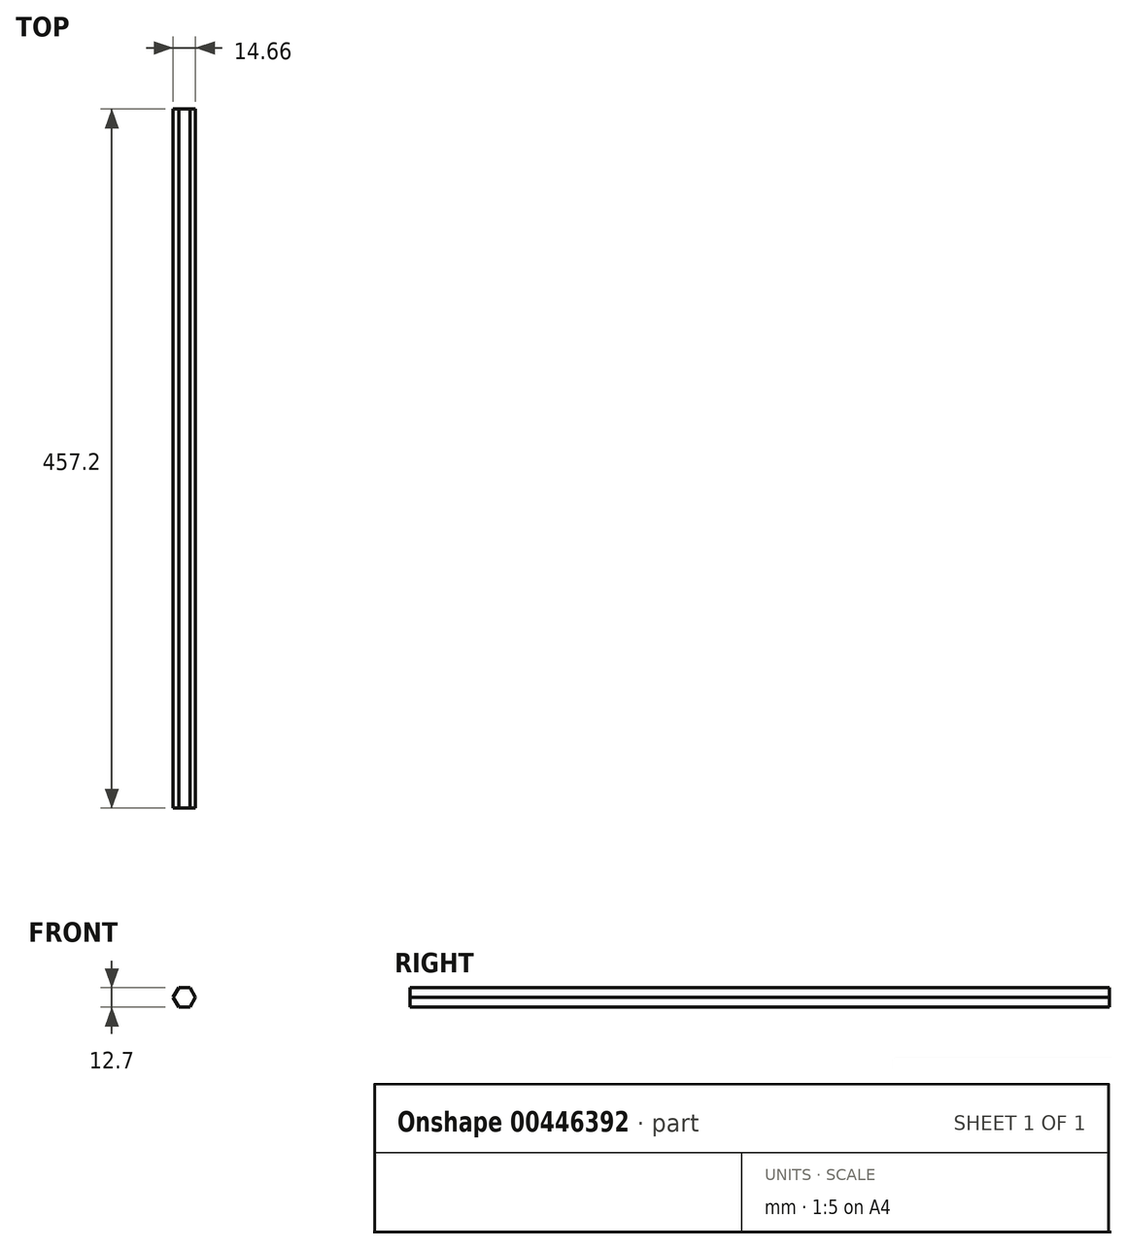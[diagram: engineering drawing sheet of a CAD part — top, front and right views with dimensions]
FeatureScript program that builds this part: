
annotation { "Feature Type Name" : "Feature", "Feature Type Description" : "" }
export const myFeature = defineFeature(function(context is Context, id is Id, definition is map)
    precondition{}
    {
        {
            var Q0;
            Q0=qCreatedBy(makeId("Front.planeOp"),FACE);
            var sketch = newSketch(context, id + "F0", { "sketchPlane" : qUnion([Q0])});
            skCircle(sketch, "E0.cCircle", {"center": v(0, 0) * mm, "radius": 6.35 * mm, "construction": true});
            skLineSegment(sketch, "E0.0", {"start": v(3.67, -6.35) * mm, "end": v(-3.67, -6.35) * mm});
            skLineSegment(sketch, "E0.1", {"start": v(-3.67, -6.35) * mm, "end": v(-7.33, 0) * mm});
            skLineSegment(sketch, "E0.2", {"start": v(-7.33, 0) * mm, "end": v(-3.67, 6.35) * mm});
            skLineSegment(sketch, "E0.3", {"start": v(-3.67, 6.35) * mm, "end": v(3.67, 6.35) * mm});
            skLineSegment(sketch, "E0.4", {"start": v(3.67, 6.35) * mm, "end": v(7.33, 0) * mm});
            skLineSegment(sketch, "E0.5", {"start": v(7.33, 0) * mm, "end": v(3.67, -6.35) * mm});
            skPoint(sketch, "E0.0.midPoint", {"position": v(0, -6.35) * mm});
            skSolve(sketch);
        }
        {
            var Q0;
            Q0=makeQuery(id+"F0.imprint","IMPRINT",FACE,{"disambiguationData":[TD([[makeQuery(id+"F0.imprint","IMPRINT",EDGE,{"derivedFrom":sQuery(id+"F0.wireOp",EDGE,"E0.0")}),-1.0]])]});
            extrude(context, id + "F1", {"entities" : qUnion([Q0]), "depth" : 457.2 * mm, "offsetDistance" : 25.4 * mm, "symmetric" : true});
        }
    });
